# Revit family: Tyco_Valve_TJR_OS&Y_6inch_FxF_TJRX1500001_Native
name_source: partatom
category: Pipe Accessories
revit_build: Autodesk Revit 2016 (Build: 20150220_1215(x64)
units: mm (PartAtom-declared; Revit-internal decimal feet)

## family parameters
Always vertical = Yes
Cut with Voids When Loaded = No
OmniClass Number = 23.65.55.14.17
OmniClass Title = Adjusting/Controlling Valves for Liquid Services
Part Type = Valve - Breaks Into
Round Connector Dimension = Use Diameter
Shared = No
Work Plane-Based = No

## types (1)
- Tyco_Valve_TJR_OS&Y_6inch_FxF_TJRX1500001_Native
    COBie = Yes
    COBie.Component.Description = Gate Valves FxF DN150 (F)
    COBie.Component.Name = Valves:Gate Valves FxF
    COBie.Type = Yes
    COBie.Type.AssetType = Fixed
    COBie.Type.Category = Pe_65_54_95_97:Valves
    COBie.Type.Manufacturer = Tyco Fire Protection Products
    COBie.Type.Material = Ductile Iron
    COBie.Type.ModelNumber = TJRX1500001
    COBie.Type.ModelReference = Gate Valves FxF DN150 (F)
    COBie.Type.NominalHeight = 0' - 0"
    COBie.Type.NominalLength = 0' - 0"
    COBie.Type.NominalWidth = 0' - 0"
    COBie.Type.ReplacementCost = 0 $
    COBie.Type.Size = 6"(DN150) x 6"(DN150)
    COBie.Type.WarrantyGuarantorParts = http://tycofsbp.com
TFPPTerms_of_Sale.pdf
    Description = Model TJR Resilient seated Gate valve OS&Y 6" (DN150(168.3)) with FxF DIN_TJRX1500001
    Finish_ = Tyco - Epoxy coating
    Flange Diameter 1 = 11"
    Flange Diameter 2 = 11"
    Length X = 11"
    Length Y = 30"
    Manufacturer = Tyco Fire Protection Products
    Manufacturer URL = www.tyco-fire.com
    Material_ = Ductile Iron
    Model = OS&Y Gate FxF - Resilient seated
    Nominal Diameter 1 = 6"
    Nominal Diameter 2 = 6"
    Outside Diameter 1 = 7"
    Outside Diameter 2 = 7"
    Part No = TJRX1500001
    Style Id = 0
    Takeout 1 = 0"
    Takeout 2 = 0"
    Technical Data Sheet No = TFP1541

## geometry (parser evidence)
native form markers: Blend x2, Sweep x71
no freeform markers — native parametric forms only
